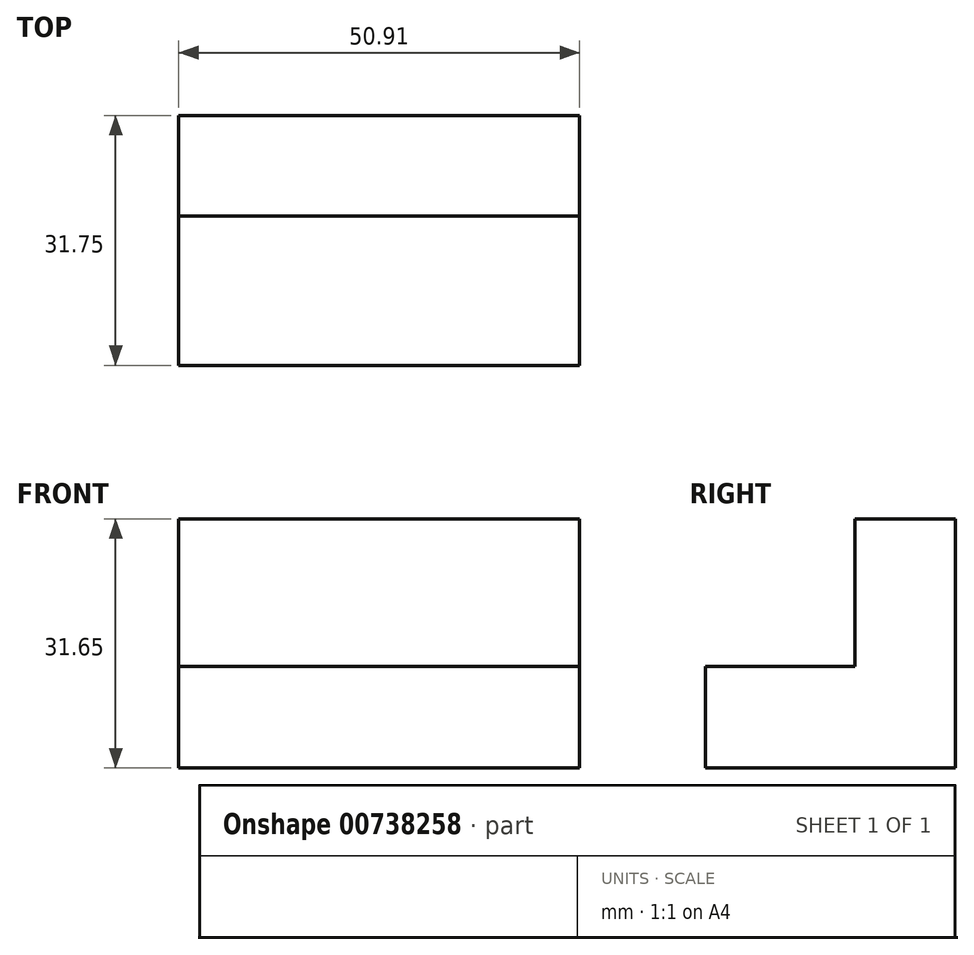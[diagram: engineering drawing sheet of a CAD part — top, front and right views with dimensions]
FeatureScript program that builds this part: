
annotation { "Feature Type Name" : "Feature", "Feature Type Description" : "" }
export const myFeature = defineFeature(function(context is Context, id is Id, definition is map)
    precondition{}
    {
        {
            var Q0;
            Q0=qCreatedBy(makeId("Front.planeOp"),FACE);
            var sketch = newSketch(context, id + "F0", { "sketchPlane" : qUnion([Q0])});
            skLineSegment(sketch, "E0", {"start": v(0, 0) * mm, "end": v(-50.91, 0) * mm});
            skLineSegment(sketch, "E1", {"start": v(-50.91, 0) * mm, "end": v(-50.91, 31.65) * mm});
            skLineSegment(sketch, "E2", {"start": v(-50.91, 31.65) * mm, "end": v(0, 31.65) * mm});
            skLineSegment(sketch, "E3", {"start": v(0, 31.65) * mm, "end": v(0, 0) * mm});
            skSolve(sketch);
        }
        {
            var Q0;
            Q0 = qSketchRegion(id + "F0", true);
            extrude(context, id + "F1", {"entities" : qUnion([Q0]), "depth" : 31.75 * mm, "offsetDistance" : 25.4 * mm});
        }
        {
            var Q0;
            Q0=makeQuery(id+"F1.opExtrude","SWEPT_FACE",FACE,{"disambiguationData":[OSD([sQuery(id+"F0.wireOp",EDGE,"E3")])]});
            var sketch = newSketch(context, id + "F2", { "sketchPlane" : qUnion([Q0])});
            skLineSegment(sketch, "E4", {"start": v(-12.8, 12.9) * mm, "end": v(-31.75, 12.9) * mm});
            skLineSegment(sketch, "E5", {"start": v(-12.8, 12.9) * mm, "end": v(-12.8, 31.65) * mm});
            skSolve(sketch);
        }
        {
            var Q0;
            {var subQ0=sQuery(id+"F2.wireOp",EDGE,"E4");Q0=makeQuery(id+"F2.imprint","IMPRINT",FACE,{"disambiguationData":[TD([[makeQuery(id+"F2.imprint","IMPRINT",EDGE,{"derivedFrom":subQ0}),-1.0]])]});}
            extrude(context, id + "F3", {"entities" : qUnion([Q0]), "operationType" : NewBodyOperationType.REMOVE, "endBound" : BoundingType.THROUGH_ALL, "oppositeDirection" : true, "depth" : 25.4 * mm, "offsetDistance" : 25.4 * mm});
        }
    });
